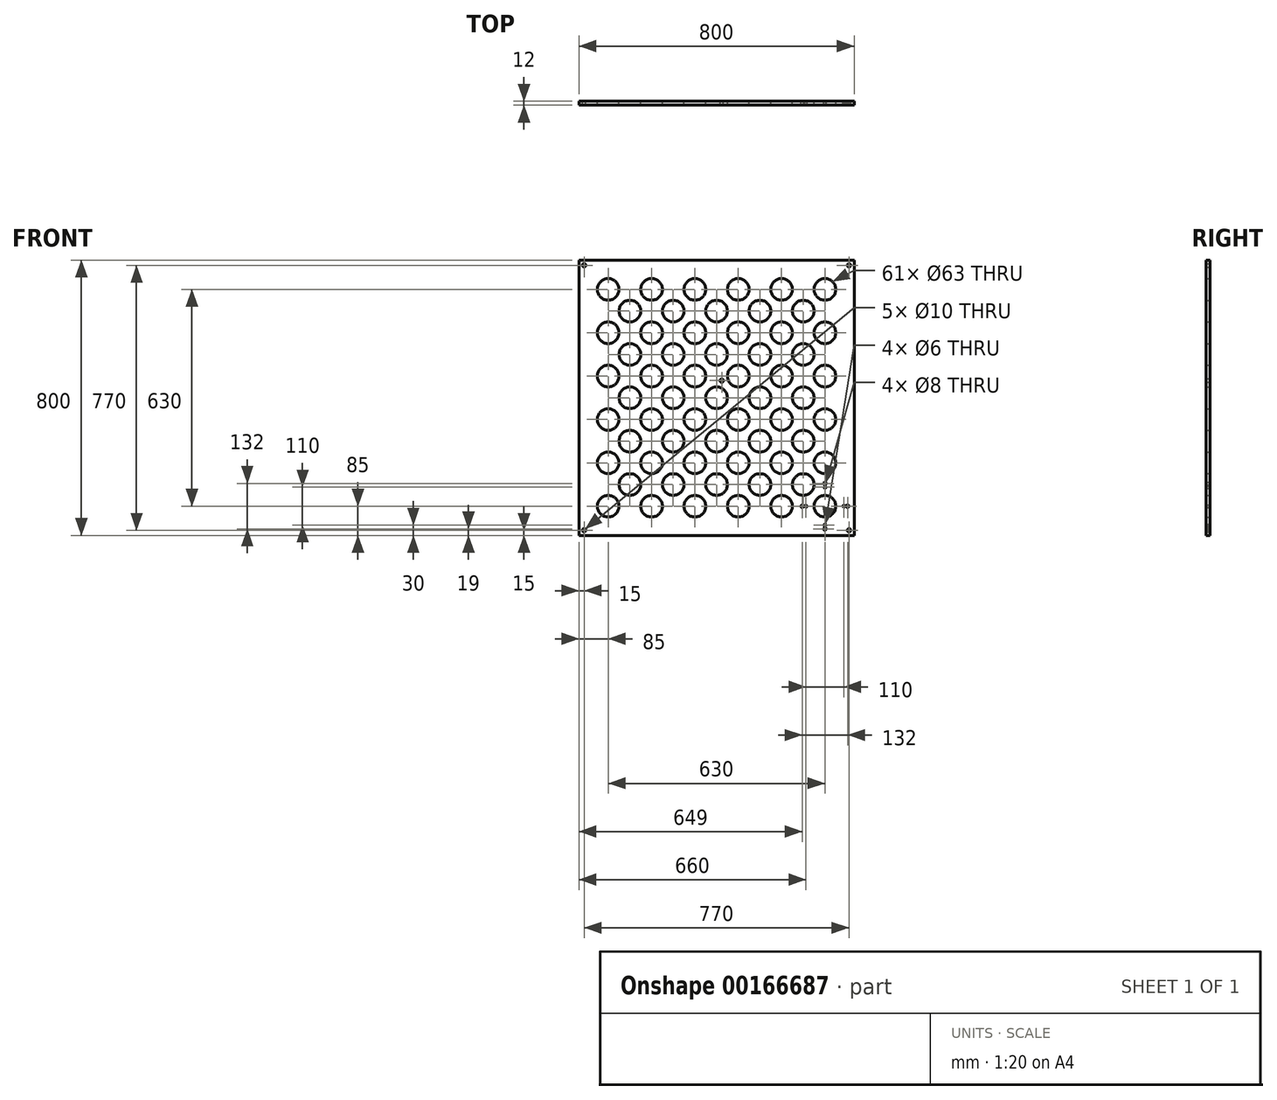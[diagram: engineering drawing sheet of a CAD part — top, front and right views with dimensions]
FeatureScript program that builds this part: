
annotation { "Feature Type Name" : "Feature", "Feature Type Description" : "" }
export const myFeature = defineFeature(function(context is Context, id is Id, definition is map)
    precondition{}
    {
        {
            var Q0;
            Q0=qCreatedBy(makeId("Front.planeOp"),FACE);
            var sketch = newSketch(context, id + "F0", { "sketchPlane" : qUnion([Q0])});
            skLineSegment(sketch, "E0.bottom", {"start": v(400, -400) * mm, "end": v(-400, -400) * mm});
            skLineSegment(sketch, "E0.top", {"start": v(400, 400) * mm, "end": v(-400, 400) * mm});
            skLineSegment(sketch, "E0.left", {"start": v(400, -400) * mm, "end": v(400, 400) * mm});
            skLineSegment(sketch, "E0.right", {"start": v(-400, -400) * mm, "end": v(-400, 400) * mm});
            skPoint(sketch, "E0.middle", {"position": v(0, 0) * mm});
            skCircle(sketch, "E1", {"center": v(-315, -315) * mm, "radius": 31.5 * mm});
            skCircle(sketch, "E2", {"center": v(-252, -252) * mm, "radius": 31.5 * mm});
            skCircle(sketch, "E3.0.1.0", {"center": v(-315, -189) * mm, "radius": 31.5 * mm});
            skCircle(sketch, "E3.0.2.0", {"center": v(-315, -63) * mm, "radius": 31.5 * mm});
            skCircle(sketch, "E3.0.3.0", {"center": v(-315, 63) * mm, "radius": 31.5 * mm});
            skCircle(sketch, "E3.0.4.0", {"center": v(-315, 189) * mm, "radius": 31.5 * mm});
            skCircle(sketch, "E3.0.5.0", {"center": v(-315, 315) * mm, "radius": 31.5 * mm});
            skCircle(sketch, "E3.1.0.0", {"center": v(-189, -315) * mm, "radius": 31.5 * mm});
            skCircle(sketch, "E3.1.1.0", {"center": v(-189, -189) * mm, "radius": 31.5 * mm});
            skCircle(sketch, "E3.1.2.0", {"center": v(-189, -63) * mm, "radius": 31.5 * mm});
            skCircle(sketch, "E3.1.3.0", {"center": v(-189, 63) * mm, "radius": 31.5 * mm});
            skCircle(sketch, "E3.1.4.0", {"center": v(-189, 189) * mm, "radius": 31.5 * mm});
            skCircle(sketch, "E3.1.5.0", {"center": v(-189, 315) * mm, "radius": 31.5 * mm});
            skCircle(sketch, "E3.2.0.0", {"center": v(-63, -315) * mm, "radius": 31.5 * mm});
            skCircle(sketch, "E3.2.1.0", {"center": v(-63, -189) * mm, "radius": 31.5 * mm});
            skCircle(sketch, "E3.2.2.0", {"center": v(-63, -63) * mm, "radius": 31.5 * mm});
            skCircle(sketch, "E3.2.3.0", {"center": v(-63, 63) * mm, "radius": 31.5 * mm});
            skCircle(sketch, "E3.2.4.0", {"center": v(-63, 189) * mm, "radius": 31.5 * mm});
            skCircle(sketch, "E3.2.5.0", {"center": v(-63, 315) * mm, "radius": 31.5 * mm});
            skCircle(sketch, "E3.3.0.0", {"center": v(63, -315) * mm, "radius": 31.5 * mm});
            skCircle(sketch, "E3.3.1.0", {"center": v(63, -189) * mm, "radius": 31.5 * mm});
            skCircle(sketch, "E3.3.2.0", {"center": v(63, -63) * mm, "radius": 31.5 * mm});
            skCircle(sketch, "E3.3.3.0", {"center": v(63, 63) * mm, "radius": 31.5 * mm});
            skCircle(sketch, "E3.3.4.0", {"center": v(63, 189) * mm, "radius": 31.5 * mm});
            skCircle(sketch, "E3.3.5.0", {"center": v(63, 315) * mm, "radius": 31.5 * mm});
            skCircle(sketch, "E3.4.0.0", {"center": v(189, -315) * mm, "radius": 31.5 * mm});
            skCircle(sketch, "E3.4.1.0", {"center": v(189, -189) * mm, "radius": 31.5 * mm});
            skCircle(sketch, "E3.4.2.0", {"center": v(189, -63) * mm, "radius": 31.5 * mm});
            skCircle(sketch, "E3.4.3.0", {"center": v(189, 63) * mm, "radius": 31.5 * mm});
            skCircle(sketch, "E3.4.4.0", {"center": v(189, 189) * mm, "radius": 31.5 * mm});
            skCircle(sketch, "E3.4.5.0", {"center": v(189, 315) * mm, "radius": 31.5 * mm});
            skCircle(sketch, "E3.5.0.0", {"center": v(315, -315) * mm, "radius": 31.5 * mm});
            skCircle(sketch, "E3.5.1.0", {"center": v(315, -189) * mm, "radius": 31.5 * mm});
            skCircle(sketch, "E3.5.2.0", {"center": v(315, -63) * mm, "radius": 31.5 * mm});
            skCircle(sketch, "E3.5.3.0", {"center": v(315, 63) * mm, "radius": 31.5 * mm});
            skCircle(sketch, "E3.5.4.0", {"center": v(315, 189) * mm, "radius": 31.5 * mm});
            skCircle(sketch, "E3.5.5.0", {"center": v(315, 315) * mm, "radius": 31.5 * mm});
            skLineSegment(sketch, "E3.direction1", {"start": v(-315, -315) * mm, "end": v(-189, -315) * mm, "construction": true});
            skLineSegment(sketch, "E3.direction2", {"start": v(-315, -315) * mm, "end": v(-315, -189) * mm, "construction": true});
            skCircle(sketch, "E4.0.1.0", {"center": v(-252, -126) * mm, "radius": 31.5 * mm});
            skCircle(sketch, "E4.0.2.0", {"center": v(-252, 0) * mm, "radius": 31.5 * mm});
            skCircle(sketch, "E4.0.3.0", {"center": v(-252, 126) * mm, "radius": 31.5 * mm});
            skCircle(sketch, "E4.0.4.0", {"center": v(-252, 252) * mm, "radius": 31.5 * mm});
            skCircle(sketch, "E4.1.0.0", {"center": v(-126, -252) * mm, "radius": 31.5 * mm});
            skCircle(sketch, "E4.1.1.0", {"center": v(-126, -126) * mm, "radius": 31.5 * mm});
            skCircle(sketch, "E4.1.2.0", {"center": v(-126, 0) * mm, "radius": 31.5 * mm});
            skCircle(sketch, "E4.1.3.0", {"center": v(-126, 126) * mm, "radius": 31.5 * mm});
            skCircle(sketch, "E4.1.4.0", {"center": v(-126, 252) * mm, "radius": 31.5 * mm});
            skCircle(sketch, "E4.2.0.0", {"center": v(0, -252) * mm, "radius": 31.5 * mm});
            skCircle(sketch, "E4.2.1.0", {"center": v(0, -126) * mm, "radius": 31.5 * mm});
            skCircle(sketch, "E4.2.2.0", {"center": v(0, 0) * mm, "radius": 31.5 * mm});
            skCircle(sketch, "E4.2.3.0", {"center": v(0, 126) * mm, "radius": 31.5 * mm});
            skCircle(sketch, "E4.2.4.0", {"center": v(0, 252) * mm, "radius": 31.5 * mm});
            skCircle(sketch, "E4.3.0.0", {"center": v(126, -252) * mm, "radius": 31.5 * mm});
            skCircle(sketch, "E4.3.1.0", {"center": v(126, -126) * mm, "radius": 31.5 * mm});
            skCircle(sketch, "E4.3.2.0", {"center": v(126, 0) * mm, "radius": 31.5 * mm});
            skCircle(sketch, "E4.3.3.0", {"center": v(126, 126) * mm, "radius": 31.5 * mm});
            skCircle(sketch, "E4.3.4.0", {"center": v(126, 252) * mm, "radius": 31.5 * mm});
            skCircle(sketch, "E4.4.0.0", {"center": v(252, -252) * mm, "radius": 31.5 * mm});
            skCircle(sketch, "E4.4.1.0", {"center": v(252, -126) * mm, "radius": 31.5 * mm});
            skCircle(sketch, "E4.4.2.0", {"center": v(252, 0) * mm, "radius": 31.5 * mm});
            skCircle(sketch, "E4.4.3.0", {"center": v(252, 126) * mm, "radius": 31.5 * mm});
            skCircle(sketch, "E4.4.4.0", {"center": v(252, 252) * mm, "radius": 31.5 * mm});
            skLineSegment(sketch, "E4.direction1", {"start": v(-252, -252) * mm, "end": v(-126, -252) * mm, "construction": true});
            skLineSegment(sketch, "E4.direction2", {"start": v(-252, -252) * mm, "end": v(-252, -126) * mm, "construction": true});
            skSolve(sketch);
        }
        {
            var Q0;
            Q0 = qSketchRegion(id + "F0", true);
            extrude(context, id + "F1", {"entities" : qUnion([Q0]), "depth" : 12 * mm});
        }
        {
            var Q0;
            Q0=qCreatedBy(makeId("Front.planeOp"),FACE);
            var sketch = newSketch(context, id + "F2", { "sketchPlane" : qUnion([Q0])});
            skCircle(sketch, "E5", {"center": v(315, -381) * mm, "radius": 4 * mm});
            skCircle(sketch, "E6.1.0", {"center": v(381, -315) * mm, "radius": 4 * mm});
            skCircle(sketch, "E6.2.0", {"center": v(315, -249) * mm, "radius": 4 * mm});
            skCircle(sketch, "E6.3.0", {"center": v(249, -315) * mm, "radius": 4 * mm});
            skPoint(sketch, "E6.center", {"position": v(315, -315) * mm});
            skCircle(sketch, "E7", {"center": v(315, -370) * mm, "radius": 3 * mm});
            skCircle(sketch, "E8.1.0", {"center": v(370, -315) * mm, "radius": 3 * mm});
            skCircle(sketch, "E8.2.0", {"center": v(315, -260) * mm, "radius": 3 * mm});
            skCircle(sketch, "E8.3.0", {"center": v(260, -315) * mm, "radius": 3 * mm});
            skSolve(sketch);
        }
        {
            var Q0;
            Q0 = qSketchRegion(id + "F2", true);
            extrude(context, id + "F3", {"entities" : qUnion([Q0]), "operationType" : NewBodyOperationType.REMOVE, "endBound" : BoundingType.THROUGH_ALL, "depth" : 25 * mm});
        }
        {
            var Q0;
            Q0=qCreatedBy(makeId("Front.planeOp"),FACE);
            var sketch = newSketch(context, id + "F4", { "sketchPlane" : qUnion([Q0])});
            skCircle(sketch, "E9", {"center": v(-385, -385) * mm, "radius": 5 * mm});
            skCircle(sketch, "E10.0.1.0", {"center": v(-385, 385) * mm, "radius": 5 * mm});
            skCircle(sketch, "E10.1.0.0", {"center": v(385, -385) * mm, "radius": 5 * mm});
            skCircle(sketch, "E10.1.1.0", {"center": v(385, 385) * mm, "radius": 5 * mm});
            skLineSegment(sketch, "E10.direction1", {"start": v(-385, -385) * mm, "end": v(385, -385) * mm, "construction": true});
            skLineSegment(sketch, "E10.direction2", {"start": v(-385, -385) * mm, "end": v(-385, 385) * mm, "construction": true});
            skCircle(sketch, "E11", {"center": v(15, 50) * mm, "radius": 5 * mm});
            skSolve(sketch);
        }
        {
            var Q0;
            Q0 = qSketchRegion(id + "F4", true);
            extrude(context, id + "F5", {"entities" : qUnion([Q0]), "operationType" : NewBodyOperationType.REMOVE, "endBound" : BoundingType.THROUGH_ALL, "depth" : 25 * mm});
        }
    });
